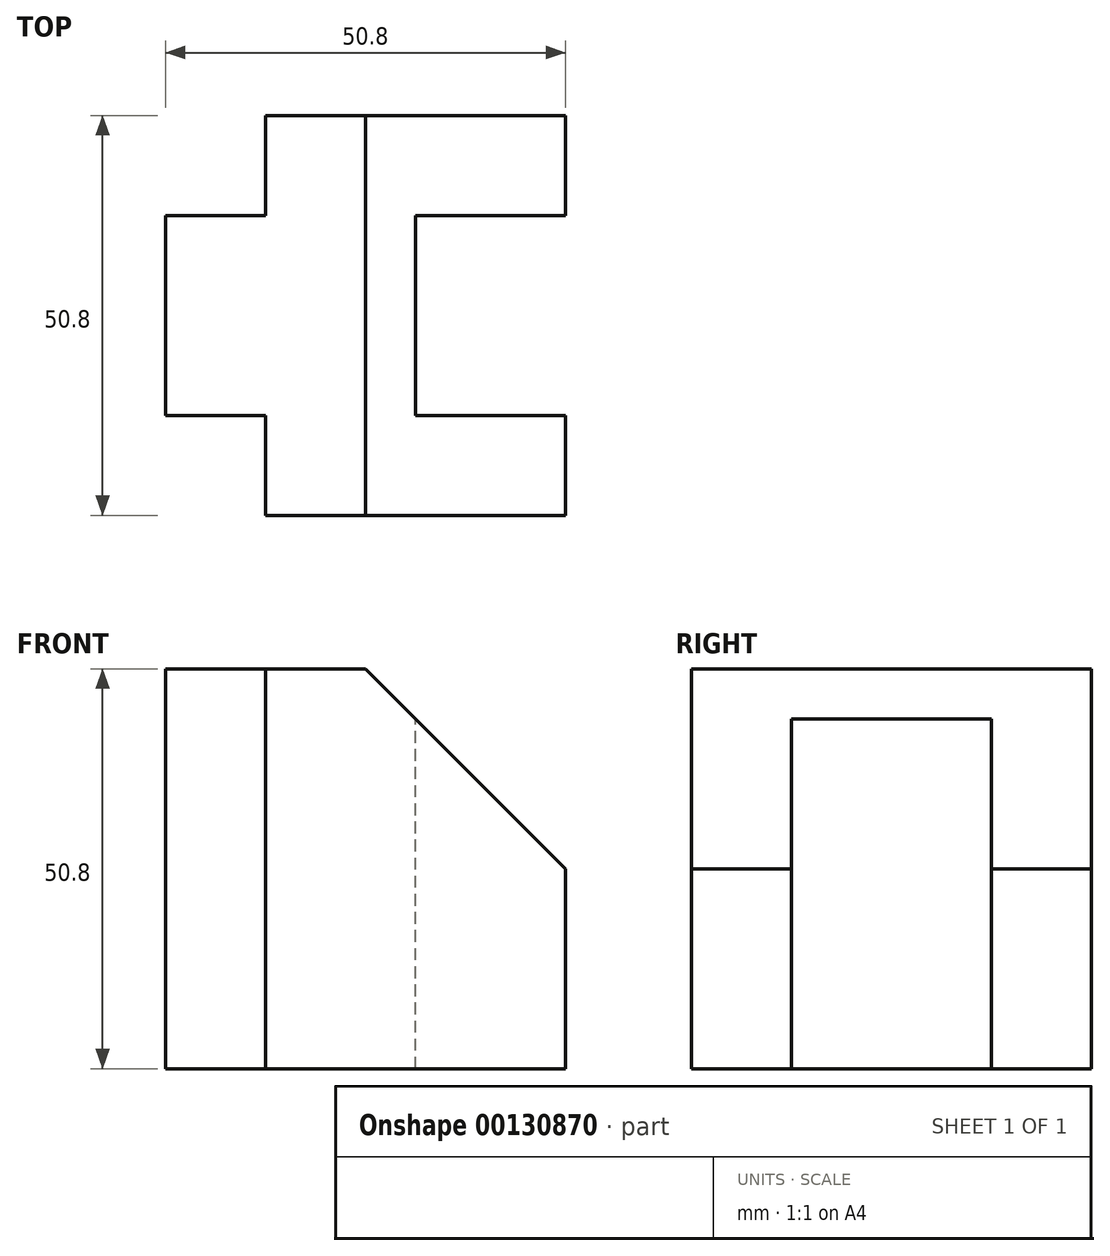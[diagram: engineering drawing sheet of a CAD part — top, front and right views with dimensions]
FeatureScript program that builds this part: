
annotation { "Feature Type Name" : "Feature", "Feature Type Description" : "" }
export const myFeature = defineFeature(function(context is Context, id is Id, definition is map)
    precondition{}
    {
        {
            var Q0;
            Q0=qCreatedBy(makeId("Top.planeOp"),FACE);
            var sketch = newSketch(context, id + "F0", { "sketchPlane" : qUnion([Q0])});
            skLineSegment(sketch, "E0.bottom", {"start": v(0, 0) * mm, "end": v(50.8, 0) * mm});
            skLineSegment(sketch, "E0.top", {"start": v(0, 50.8) * mm, "end": v(50.8, 50.8) * mm});
            skLineSegment(sketch, "E0.left", {"start": v(0, 0) * mm, "end": v(0, 50.8) * mm});
            skLineSegment(sketch, "E0.right", {"start": v(50.8, 0) * mm, "end": v(50.8, 50.8) * mm});
            skSolve(sketch);
        }
        {
            var Q0;
            Q0 = qSketchRegion(id + "F0", true);
            extrude(context, id + "F1", {"entities" : qUnion([Q0]), "oppositeDirection" : true, "depth" : 50.8 * mm});
        }
        {
            var Q0;
            Q0=qCreatedBy(makeId("Top.planeOp"),FACE);
            var sketch = newSketch(context, id + "F2", { "sketchPlane" : qUnion([Q0])});
            skLineSegment(sketch, "E1.bottom", {"start": v(50.8, 12.7) * mm, "end": v(31.75, 12.7) * mm});
            skLineSegment(sketch, "E1.top", {"start": v(50.8, 38.1) * mm, "end": v(31.75, 38.1) * mm});
            skLineSegment(sketch, "E1.left", {"start": v(50.8, 12.7) * mm, "end": v(50.8, 38.1) * mm});
            skLineSegment(sketch, "E1.right", {"start": v(31.75, 12.7) * mm, "end": v(31.75, 38.1) * mm});
            skLineSegment(sketch, "E2.bottom", {"start": v(0, 0) * mm, "end": v(12.7, 0) * mm});
            skLineSegment(sketch, "E2.top", {"start": v(0, 12.7) * mm, "end": v(12.7, 12.7) * mm});
            skLineSegment(sketch, "E2.left", {"start": v(0, 0) * mm, "end": v(0, 12.7) * mm});
            skLineSegment(sketch, "E2.right", {"start": v(12.7, 0) * mm, "end": v(12.7, 12.7) * mm});
            skLineSegment(sketch, "E3.bottom", {"start": v(0, 50.8) * mm, "end": v(12.7, 50.8) * mm});
            skLineSegment(sketch, "E3.top", {"start": v(0, 38.1) * mm, "end": v(12.7, 38.1) * mm});
            skLineSegment(sketch, "E3.left", {"start": v(0, 50.8) * mm, "end": v(0, 38.1) * mm});
            skLineSegment(sketch, "E3.right", {"start": v(12.7, 50.8) * mm, "end": v(12.7, 38.1) * mm});
            skSolve(sketch);
        }
        {
            var Q0;
            Q0 = qSketchRegion(id + "F2", true);
            extrude(context, id + "F3", {"entities" : qUnion([Q0]), "operationType" : NewBodyOperationType.REMOVE, "endBound" : BoundingType.THROUGH_ALL, "oppositeDirection" : true, "depth" : 25.4 * mm});
        }
        {
            var Q0;
            Q0=qCreatedBy(makeId("Front.planeOp"),FACE);
            var sketch = newSketch(context, id + "F4", { "sketchPlane" : qUnion([Q0])});
            skLineSegment(sketch, "E4", {"start": v(50.8, 0) * mm, "end": v(50.8, -25.4) * mm});
            skLineSegment(sketch, "E5", {"start": v(50.8, -25.4) * mm, "end": v(25.4, 0) * mm});
            skLineSegment(sketch, "E6", {"start": v(25.4, 0) * mm, "end": v(50.8, 0) * mm});
            skSolve(sketch);
        }
        {
            var Q0;
            Q0 = qSketchRegion(id + "F4", true);
            extrude(context, id + "F5", {"entities" : qUnion([Q0]), "operationType" : NewBodyOperationType.REMOVE, "endBound" : BoundingType.THROUGH_ALL, "oppositeDirection" : true, "depth" : 25.4 * mm});
        }
    });
